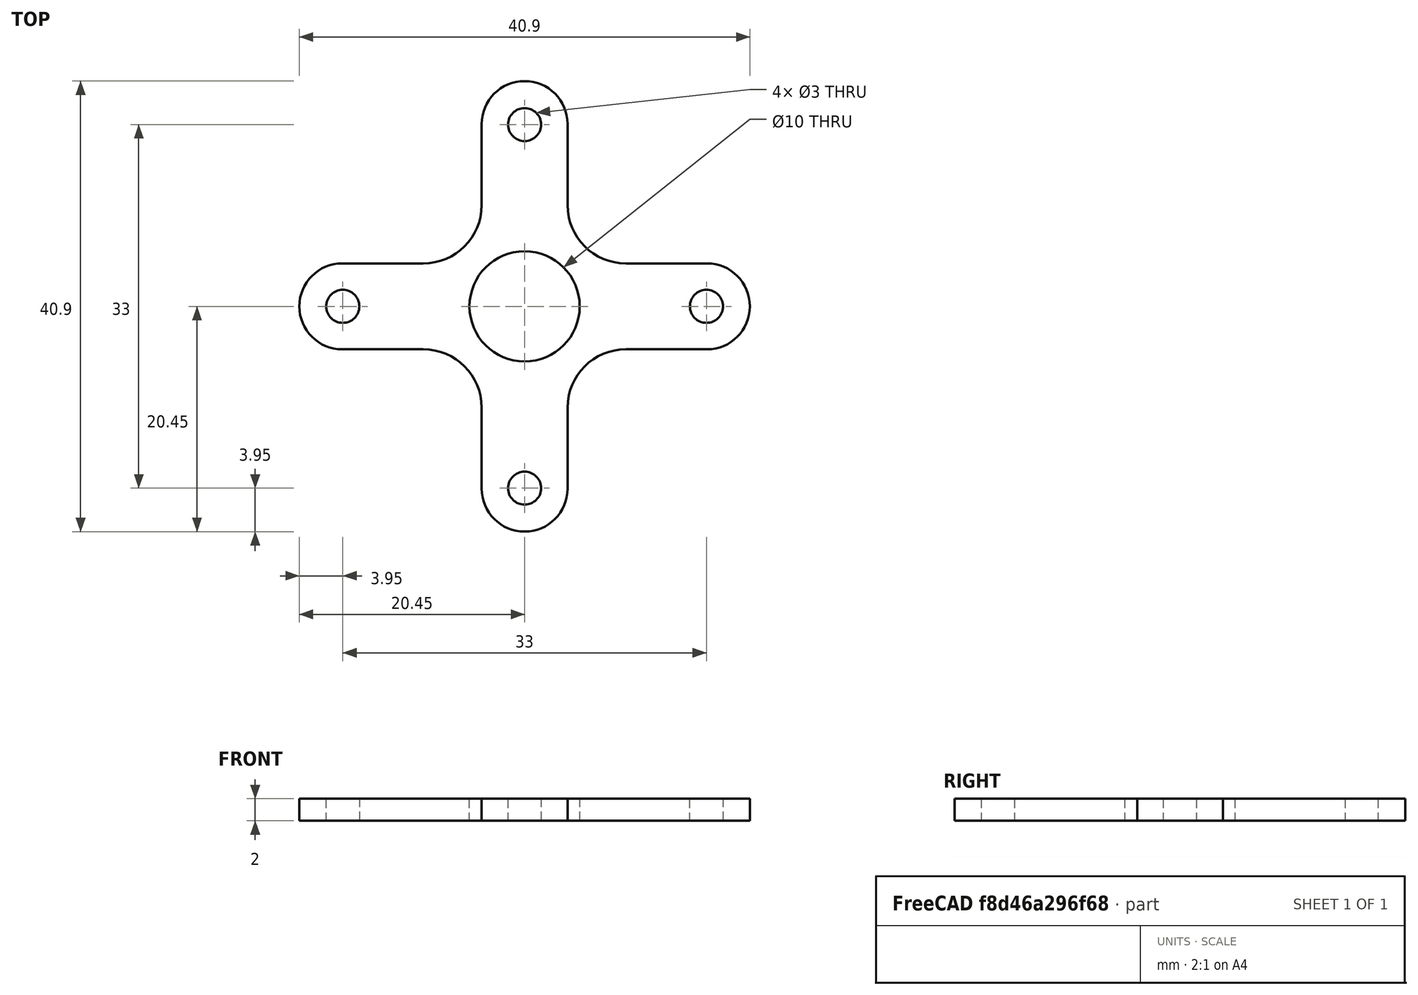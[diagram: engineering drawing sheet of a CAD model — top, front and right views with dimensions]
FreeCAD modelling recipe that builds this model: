
FCSTD DOCUMENT  (FreeCAD 0.17R13543 (Git))
Label: A2213_bracket
License: All rights reserved
LicenseURL: http://en.wikipedia.org/wiki/All_rights_reserved
objects: Sketcher::SketchObject×1, PartDesign::Pad×1, PartDesign::Body×1, App::Part×1
note: 4 computed .brp shape members not serialized (recipe doc carries the construction recipe); baked Part::Feature solids carry a one-line shape summary decoded from their .brp

FEATURE [Sketcher::SketchObject] Sketch
  MapMode = 5
  Support = -> [XY_Plane001]
  expr: Constraints[59] = 41.799999999999997 / 2 - Constraints.arm_width / 2mm
  expr: Constraints[43] = Constraints.arm_width
  expr: Constraints[12] = Constraints.hold_dia
  expr: Constraints[11] = Constraints.hold_dia
  expr: Constraints[10] = Constraints.hold_dia
  sketch-geometry (40):
    g0: Circle CenterX=0 CenterY=0 CenterZ=0 NormalX=0 NormalY=0 NormalZ=1 AngleXU=0 Radius=5
    g1: Circle [constr] CenterX=0 CenterY=0 CenterZ=0 NormalX=0 NormalY=0 NormalZ=1 AngleXU=0 Radius=16.5
    g2: Circle CenterX=0 CenterY=16.5 CenterZ=0 NormalX=0 NormalY=0 NormalZ=1 AngleXU=0 Radius=1.5
    g3: Circle CenterX=16.5 CenterY=0 CenterZ=0 NormalX=0 NormalY=0 NormalZ=1 AngleXU=0 Radius=1.5
    g4: Circle CenterX=0 CenterY=-16.5 CenterZ=0 NormalX=0 NormalY=0 NormalZ=1 AngleXU=0 Radius=1.5
    g5: Circle CenterX=-16.5 CenterY=0 CenterZ=0 NormalX=0 NormalY=0 NormalZ=1 AngleXU=0 Radius=1.5
    g6: Circle [constr] CenterX=0 CenterY=0 CenterZ=0 NormalX=0 NormalY=0 NormalZ=1 AngleXU=0 Radius=17
    g7: LineSegment [constr] StartX=-16.5466 StartY=-3.9 StartZ=0 EndX=16.5466 EndY=-3.9 EndZ=0
    g8: LineSegment [constr] StartX=16.5466 StartY=-3.9 StartZ=0 EndX=16.5466 EndY=3.9 EndZ=0
    g9: LineSegment [constr] StartX=16.5466 StartY=3.9 StartZ=0 EndX=-16.5466 EndY=3.9 EndZ=0
    g10: LineSegment [constr] StartX=-16.5466 StartY=3.9 StartZ=0 EndX=-16.5466 EndY=-3.9 EndZ=0
    g11: GeomPoint X=-16.5466 Y=0 Z=0
    g12: LineSegment [constr] StartX=-3.9 StartY=-16.5466 StartZ=0 EndX=3.9 EndY=-16.5466 EndZ=0
    g13: LineSegment [constr] StartX=3.9 StartY=-16.5466 StartZ=0 EndX=3.9 EndY=16.5466 EndZ=0
    g14: LineSegment [constr] StartX=3.9 StartY=16.5466 StartZ=0 EndX=-3.9 EndY=16.5466 EndZ=0
    g15: LineSegment [constr] StartX=-3.9 StartY=16.5466 StartZ=0 EndX=-3.9 EndY=-16.5466 EndZ=0
    g16: GeomPoint X=0 Y=16.5466 Z=0
    g17: ArcOfCircle CenterX=-16.5466 CenterY=0 CenterZ=0 NormalX=0 NormalY=0 NormalZ=1 AngleXU=0 Radius=3.9 StartAngle=1.5708 EndAngle=4.71239
    g18: GeomPoint X=16.5466 Y=0 Z=0
    g19: GeomPoint X=0 Y=-16.5466 Z=0
    g20: ArcOfCircle CenterX=0 CenterY=-16.5466 CenterZ=0 NormalX=0 NormalY=0 NormalZ=1 AngleXU=0 Radius=3.9 StartAngle=3.14159 EndAngle=6.28319
    g21: ArcOfCircle CenterX=16.5466 CenterY=0 CenterZ=0 NormalX=0 NormalY=0 NormalZ=1 AngleXU=0 Radius=3.9 StartAngle=4.71239 EndAngle=7.85398
    g22: ArcOfCircle CenterX=0 CenterY=16.5466 CenterZ=0 NormalX=0 NormalY=0 NormalZ=1 AngleXU=0 Radius=3.9 StartAngle=0 EndAngle=3.14159
    g23: LineSegment StartX=16.5466 StartY=3.9 StartZ=0 EndX=9.19239 EndY=3.9 EndZ=0
    g24: LineSegment StartX=16.5466 StartY=-3.9 StartZ=0 EndX=9.19239 EndY=-3.9 EndZ=0
    g25: LineSegment StartX=3.9 StartY=-16.5466 StartZ=0 EndX=3.9 EndY=-9.19239 EndZ=0
    g26: LineSegment StartX=-3.9 StartY=-16.5466 StartZ=0 EndX=-3.9 EndY=-9.19239 EndZ=0
    g27: LineSegment StartX=-16.5466 StartY=-3.9 StartZ=0 EndX=-9.19239 EndY=-3.9 EndZ=0
    g28: LineSegment StartX=-16.5466 StartY=3.9 StartZ=0 EndX=-9.19239 EndY=3.9 EndZ=0
    g29: LineSegment StartX=-3.9 StartY=16.5466 StartZ=0 EndX=-3.9 EndY=9.19239 EndZ=0
    g30: LineSegment StartX=3.9 StartY=16.5466 StartZ=0 EndX=3.9 EndY=9.19239 EndZ=0
    g31: ArcOfCircle CenterX=9.19239 CenterY=9.19239 CenterZ=0 NormalX=0 NormalY=0 NormalZ=1 AngleXU=0 Radius=5.29239 StartAngle=3.14159 EndAngle=4.71239
    g32: ArcOfCircle CenterX=9.19239 CenterY=-9.19239 CenterZ=0 NormalX=0 NormalY=0 NormalZ=1 AngleXU=0 Radius=5.29239 StartAngle=1.5708 EndAngle=3.14159
    g33: ArcOfCircle CenterX=-9.19239 CenterY=-9.19239 CenterZ=0 NormalX=0 NormalY=0 NormalZ=1 AngleXU=0 Radius=5.29239 StartAngle=0 EndAngle=1.5708
    g34: ArcOfCircle CenterX=-9.19239 CenterY=9.19239 CenterZ=0 NormalX=0 NormalY=0 NormalZ=1 AngleXU=0 Radius=5.29239 StartAngle=4.71239 EndAngle=6.28319
    g35: Circle [constr] CenterX=0 CenterY=0 CenterZ=0 NormalX=0 NormalY=0 NormalZ=1 AngleXU=0 Radius=13
    g36: LineSegment [constr] StartX=-9.19239 StartY=9.19239 StartZ=0 EndX=9.19239 EndY=9.19239 EndZ=0
    g37: LineSegment [constr] StartX=9.19239 StartY=9.19239 StartZ=0 EndX=9.19239 EndY=-9.19239 EndZ=0
    g38: LineSegment [constr] StartX=9.19239 StartY=-9.19239 StartZ=0 EndX=-9.19239 EndY=-9.19239 EndZ=0
    g39: LineSegment [constr] StartX=-9.19239 StartY=-9.19239 StartZ=0 EndX=-9.19239 EndY=9.19239 EndZ=0
  constraints (100):
    c: Coincident(g0,g-1)
    c: Radius(g0) = 5
    c: Coincident(g1,g-1)
    c: Radius(g1) = 16.5  'mount_hole_radius'
    c: PointOnObject(g2,g1)
    c: Vertical(g2,g-1)
    c: PointOnObject(g3,g1)
    c: PointOnObject(g4,g1)
    c: PointOnObject(g5,g1)
    c: Radius(g2) = 1.5  'hold_dia'
    c: Radius(g3) = 1.5
    c: Radius(g4) = 1.5
    c: Radius(g5) = 1.5
    c: Vertical(g-1,g4)
    c: Horizontal(g3,g-1)
    c: Horizontal(g5,g-1)
    c: Coincident(g6,g-1)
    c: Coincident(g7,g8)
    c: Coincident(g8,g9)
    c: Coincident(g9,g10)
    c: Coincident(g10,g7)
    c: Horizontal(g7)
    c: Vertical(g8)
    c: Vertical(g10)
    c: PointOnObject(g7,g6)
    c: PointOnObject(g8,g6)
    c: PointOnObject(g11,g10)
    c: Symmetric(g9,g7,g11)
    c: Horizontal(g11,g-1)
    c: Coincident(g12,g13)
    c: Coincident(g13,g14)
    c: Coincident(g14,g15)
    c: Coincident(g15,g12)
    c: Horizontal(g12)
    c: Horizontal(g14)
    c: Vertical(g13)
    c: Vertical(g15)
    c: PointOnObject(g12,g6)
    c: PointOnObject(g16,g14)
    c: PointOnObject(g13,g6)
    c: Symmetric(g14,g13,g16)
    c: Vertical(g16,g-1)
    c: DistanceY(g10,g10) = 7.8  'arm_width'
    c: DistanceX(g14,g14) = 7.8
    c: Coincident(g17,g11)
    c: Coincident(g17,g7)
    c: Coincident(g17,g9)
    c: PointOnObject(g18,g8)
    c: Symmetric(g7,g8,g18)
    c: Symmetric(g12,g12,g19)
    c: Coincident(g20,g19)
    c: Coincident(g20,g12)
    c: Coincident(g20,g12)
    c: Coincident(g21,g18)
    c: Coincident(g21,g7)
    c: Coincident(g21,g8)
    c: Coincident(g22,g16)
    c: Coincident(g22,g13)
    c: Coincident(g22,g14)
    c: Radius(g6) = 17
    c: Coincident(g23,g8)
    c: Horizontal(g23)
    c: Coincident(g24,g7)
    c: Coincident(g25,g12)
    c: Vertical(g25)
    c: Coincident(g26,g12)
    c: Vertical(g26)
    c: Coincident(g27,g7)
    c: Coincident(g28,g9)
    c: Coincident(g29,g14)
    c: Vertical(g29)
    c: Coincident(g30,g13)
    c: Vertical(g30)
    c: Tangent(g23,g31) = 1.5708
    c: Tangent(g30,g31) = -1.5708
    c: Tangent(g24,g32) = -1.5708
    c: Tangent(g25,g32) = 1.5708
    c: Tangent(g26,g33) = -1.5708
    c: Tangent(g27,g33) = 1.5708
    c: Tangent(g28,g34) = -1.5708
    c: Tangent(g29,g34) = 1.5708
    c: Coincident(g35,g-1)
    c: PointOnObject(g31,g35)
    c: PointOnObject(g32,g35)
    c: PointOnObject(g33,g35)
    c: PointOnObject(g34,g35)
    c: Coincident(g36,g37)
    c: Coincident(g37,g38)
    c: Coincident(g38,g39)
    c: Coincident(g39,g36)
    c: Horizontal(g36)
    c: Horizontal(g38)
    c: Vertical(g37)
    c: Vertical(g39)
    c: Coincident(g36,g34)
    c: Coincident(g37,g32)
    c: Coincident(g31,g36)
    c: Coincident(g38,g33)
    c: Equal(g36,g37)
    c: Radius(g35) = 13
FEATURE [PartDesign::Pad] Pad
  Length = 2
  Length2 = 100
  Profile = -> Sketch
  Reversed = true
  Type = 0
FEATURE [PartDesign::Body] Body
  Group = -> [Sketch,Pad]
  Origin = -> Origin001
  Tip = -> Pad
FEATURE [App::Part] Part
  Group = -> [Body]
  License = CC BY 3.0
  LicenseURL = http://creativecommons.org/licenses/by/3.0/
  Origin = -> Origin
